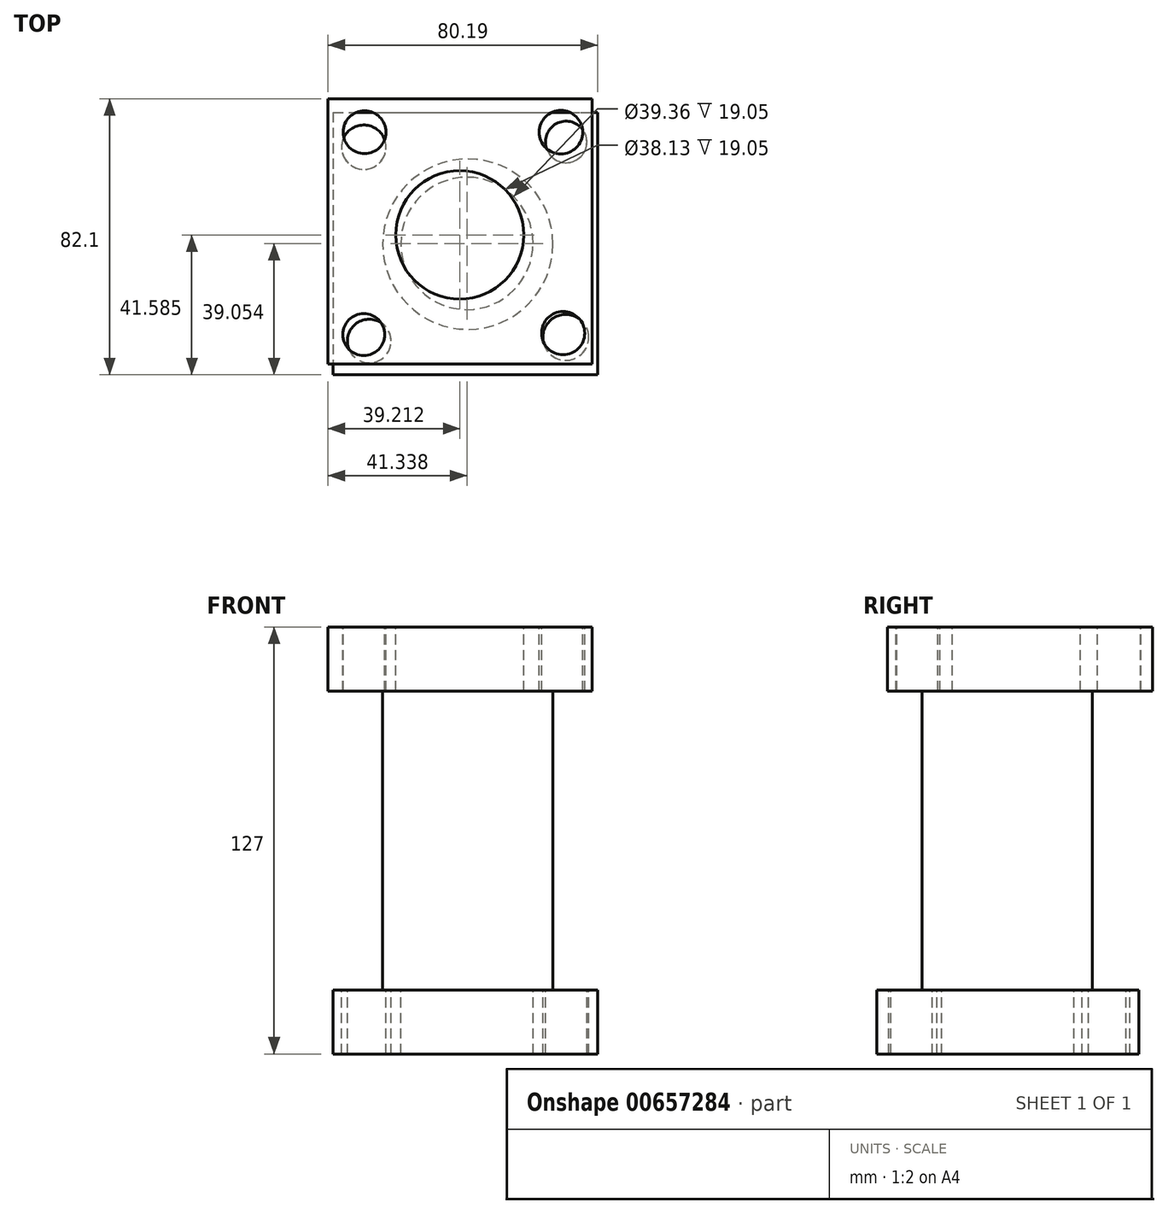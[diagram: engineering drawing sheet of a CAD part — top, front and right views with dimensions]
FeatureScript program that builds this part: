
annotation { "Feature Type Name" : "Feature", "Feature Type Description" : "" }
export const myFeature = defineFeature(function(context is Context, id is Id, definition is map)
    precondition{}
    {
        {
            var Q0;
            Q0=qCreatedBy(makeId("Top.planeOp"),FACE);
            var sketch = newSketch(context, id + "F0", { "sketchPlane" : qUnion([Q0])});
            skLineSegment(sketch, "E0.bottom", {"start": v(-51.4, 5.93) * mm, "end": v(27.22, 5.93) * mm});
            skLineSegment(sketch, "E0.top", {"start": v(-51.4, -72.12) * mm, "end": v(27.22, -72.12) * mm});
            skLineSegment(sketch, "E0.left", {"start": v(-51.4, 5.93) * mm, "end": v(-51.4, -72.12) * mm});
            skLineSegment(sketch, "E0.right", {"start": v(27.22, 5.93) * mm, "end": v(27.22, -72.12) * mm});
            skSolve(sketch);
        }
        {
            var Q0;
            Q0 = qSketchRegion(id + "F0", true);
            extrude(context, id + "F1", {"entities" : qUnion([Q0]), "depth" : 19.05 * mm, "offsetDistance" : 25.4 * mm});
        }
        {
            var Q0;
            Q0=makeQuery(id+"F1.opExtrude","CAP_FACE",FACE,{"disambiguationData":[OSD([sQuery(id+"F0.wireOp",EDGE,"E0.bottom"),sQuery(id+"F0.wireOp",EDGE,"E0.top"),sQuery(id+"F0.wireOp",EDGE,"E0.left"),sQuery(id+"F0.wireOp",EDGE,"E0.right")])],"isStart":false});
            var sketch = newSketch(context, id + "F2", { "sketchPlane" : qUnion([Q0])});
            skSolve(sketch);
        }
        {
            var Q0;
            Q0=makeQuery(id+"F2.imprint","IMPRINT",FACE,{"disambiguationData":[TD([[makeQuery(id+"F2.imprint","IMPRINT",EDGE,{"derivedFrom":makeQuery(id+"F1.opExtrude","CAP_EDGE",EDGE,{"disambiguationData":[OSD([sQuery(id+"F0.wireOp",EDGE,"E0.bottom")])],"isStart":false})}),-1.0]])]});
            var sketch = newSketch(context, id + "F3", { "sketchPlane" : qUnion([Q0])});
            skCircle(sketch, "E1", {"center": v(-42.33, -4.47) * mm, "radius": 6.6 * mm});
            skSolve(sketch);
        }
        {
            var Q0;
            Q0=makeQuery(id+"F2.imprint","IMPRINT",FACE,{"disambiguationData":[TD([[makeQuery(id+"F2.imprint","IMPRINT",EDGE,{"derivedFrom":makeQuery(id+"F1.opExtrude","CAP_EDGE",EDGE,{"disambiguationData":[OSD([sQuery(id+"F0.wireOp",EDGE,"E0.bottom")])],"isStart":false})}),-1.0]])]});
            var sketch = newSketch(context, id + "F4", { "sketchPlane" : qUnion([Q0])});
            skCircle(sketch, "E2", {"center": v(17.9, -2.9) * mm, "radius": 6.17 * mm});
            skSolve(sketch);
        }
        {
            var Q0;
            Q0=makeQuery(id+"F4.imprint","IMPRINT",FACE,{"disambiguationData":[TD([[makeQuery(id+"F4.imprint","IMPRINT",EDGE,{"derivedFrom":sQuery(id+"F4.wireOp",EDGE,"E2")}),-1.0]])]});
            var sketch = newSketch(context, id + "F5", { "sketchPlane" : qUnion([Q0])});
            skCircle(sketch, "E3", {"center": v(-40.7, -62.11) * mm, "radius": 6.5 * mm});
            skSolve(sketch);
        }
        {
            var Q0;
            Q0=makeQuery(id+"F4.imprint","IMPRINT",FACE,{"disambiguationData":[TD([[makeQuery(id+"F4.imprint","IMPRINT",EDGE,{"derivedFrom":sQuery(id+"F4.wireOp",EDGE,"E2")}),-1.0]])]});
            var sketch = newSketch(context, id + "F6", { "sketchPlane" : qUnion([Q0])});
            skCircle(sketch, "E4", {"center": v(17.8, -61.02) * mm, "radius": 6.83 * mm});
            skSolve(sketch);
        }
        {
            var Q0;
            Q0=makeQuery(id+"F2.imprint","IMPRINT",FACE,{"disambiguationData":[TD([[makeQuery(id+"F2.imprint","IMPRINT",EDGE,{"derivedFrom":makeQuery(id+"F1.opExtrude","CAP_EDGE",EDGE,{"disambiguationData":[OSD([sQuery(id+"F0.wireOp",EDGE,"E0.bottom")])],"isStart":false})}),-1.0]])]});
            var sketch = newSketch(context, id + "F7", { "sketchPlane" : qUnion([Q0])});
            skCircle(sketch, "E5", {"center": v(-11.63, -33.07) * mm, "radius": 19.68 * mm});
            skSolve(sketch);
        }
        {
            var Q0;
            Q0=makeQuery(id+"F7.imprint","IMPRINT",FACE,{"disambiguationData":[TD([[makeQuery(id+"F7.imprint","IMPRINT",EDGE,{"derivedFrom":sQuery(id+"F7.wireOp",EDGE,"E5")}),1.0]])]});
            extrude(context, id + "F8", {"entities" : qUnion([Q0]), "operationType" : NewBodyOperationType.REMOVE, "oppositeDirection" : true, "depth" : 25.4 * mm, "offsetDistance" : 25.4 * mm});
        }
        {
            var Q0;
            Q0=makeQuery(id+"F2.imprint","IMPRINT",FACE,{"disambiguationData":[TD([[makeQuery(id+"F2.imprint","IMPRINT",EDGE,{"derivedFrom":makeQuery(id+"F1.opExtrude","CAP_EDGE",EDGE,{"disambiguationData":[OSD([sQuery(id+"F0.wireOp",EDGE,"E0.bottom")])],"isStart":false})}),-1.0]])]});
            var sketch = newSketch(context, id + "F9", { "sketchPlane" : qUnion([Q0])});
            skCircle(sketch, "E6", {"center": v(-11.36, -33.28) * mm, "radius": 25.34 * mm});
            skSolve(sketch);
        }
        {
            var Q0;
            Q0 = qSketchRegion(id + "F9", true);
            extrude(context, id + "F10", {"entities" : qUnion([Q0]), "operationType" : NewBodyOperationType.ADD, "depth" : 88.9 * mm, "offsetDistance" : 25.4 * mm});
        }
        {
            var Q0;
            Q0=makeQuery(id+"F10.opExtrude","CAP_FACE",FACE,{"disambiguationData":[OSD([sQuery(id+"F9.wireOp",EDGE,"E6")])],"isStart":false});
            var sketch = newSketch(context, id + "F11", { "sketchPlane" : qUnion([Q0])});
            skLineSegment(sketch, "E7.bottom", {"start": v(25.64, -68.92) * mm, "end": v(-52.97, -68.92) * mm});
            skLineSegment(sketch, "E7.top", {"start": v(25.64, 9.98) * mm, "end": v(-52.97, 9.98) * mm});
            skLineSegment(sketch, "E7.left", {"start": v(25.64, -68.92) * mm, "end": v(25.64, 9.98) * mm});
            skLineSegment(sketch, "E7.right", {"start": v(-52.97, -68.92) * mm, "end": v(-52.97, 9.98) * mm});
            skSolve(sketch);
        }
        {
            var Q0;
            Q0 = qSketchRegion(id + "F11", true);
            extrude(context, id + "F12", {"entities" : qUnion([Q0]), "operationType" : NewBodyOperationType.ADD, "depth" : 19.05 * mm, "offsetDistance" : 25.4 * mm});
        }
        {
            var Q0;
            Q0=makeQuery(id+"F12.opExtrude","CAP_FACE",FACE,{"disambiguationData":[OSD([sQuery(id+"F11.wireOp",EDGE,"E7.bottom"),sQuery(id+"F11.wireOp",EDGE,"E7.top"),sQuery(id+"F11.wireOp",EDGE,"E7.left"),sQuery(id+"F11.wireOp",EDGE,"E7.right")])],"isStart":false});
            var sketch = newSketch(context, id + "F13", { "sketchPlane" : qUnion([Q0])});
            skCircle(sketch, "E8", {"center": v(-13.76, -30.53) * mm, "radius": 19.07 * mm});
            skSolve(sketch);
        }
        {
            var Q0;
            Q0 = qSketchRegion(id + "F13", true);
            extrude(context, id + "F14", {"entities" : qUnion([Q0]), "operationType" : NewBodyOperationType.REMOVE, "oppositeDirection" : true, "depth" : 19.05 * mm, "offsetDistance" : 25.4 * mm});
        }
        {
            var Q0;
            Q0 = qSketchRegion(id + "F6", true);
            extrude(context, id + "F15", {"entities" : qUnion([Q0]), "operationType" : NewBodyOperationType.REMOVE, "oppositeDirection" : true, "depth" : 304.8 * mm, "offsetDistance" : 25.4 * mm});
        }
        {
            var Q0;
            Q0 = qSketchRegion(id + "F4", true);
            extrude(context, id + "F16", {"entities" : qUnion([Q0]), "operationType" : NewBodyOperationType.REMOVE, "oppositeDirection" : true, "depth" : 25.4 * mm, "offsetDistance" : 25.4 * mm});
        }
        {
            var Q0;
            Q0 = qSketchRegion(id + "F3", true);
            extrude(context, id + "F17", {"entities" : qUnion([Q0]), "operationType" : NewBodyOperationType.REMOVE, "oppositeDirection" : true, "depth" : 25.4 * mm, "offsetDistance" : 25.4 * mm});
        }
        {
            var Q0;
            Q0 = qSketchRegion(id + "F5", true);
            extrude(context, id + "F18", {"entities" : qUnion([Q0]), "operationType" : NewBodyOperationType.REMOVE, "oppositeDirection" : true, "depth" : 25.4 * mm, "offsetDistance" : 25.4 * mm});
        }
        {
            var Q0;
            Q0=makeQuery(id+"F12.opExtrude","CAP_FACE",FACE,{"disambiguationData":[OSD([sQuery(id+"F11.wireOp",EDGE,"E7.bottom"),sQuery(id+"F11.wireOp",EDGE,"E7.top"),sQuery(id+"F11.wireOp",EDGE,"E7.left"),sQuery(id+"F11.wireOp",EDGE,"E7.right")])],"isStart":false});
            var sketch = newSketch(context, id + "F19", { "sketchPlane" : qUnion([Q0])});
            skCircle(sketch, "E9", {"center": v(16.33, 0) * mm, "radius": 6.48 * mm});
            skCircle(sketch, "E10", {"center": v(17, -59.76) * mm, "radius": 6.43 * mm});
            skCircle(sketch, "E11", {"center": v(-42.32, -60.18) * mm, "radius": 6.22 * mm});
            skCircle(sketch, "E12", {"center": v(-42.1, 0) * mm, "radius": 6.38 * mm});
            skSolve(sketch);
        }
        {
            var Q0;
            Q0 = qSketchRegion(id + "F19", true);
            extrude(context, id + "F20", {"entities" : qUnion([Q0]), "operationType" : NewBodyOperationType.REMOVE, "oppositeDirection" : true, "depth" : 25.4 * mm, "offsetDistance" : 25.4 * mm});
        }
    });
